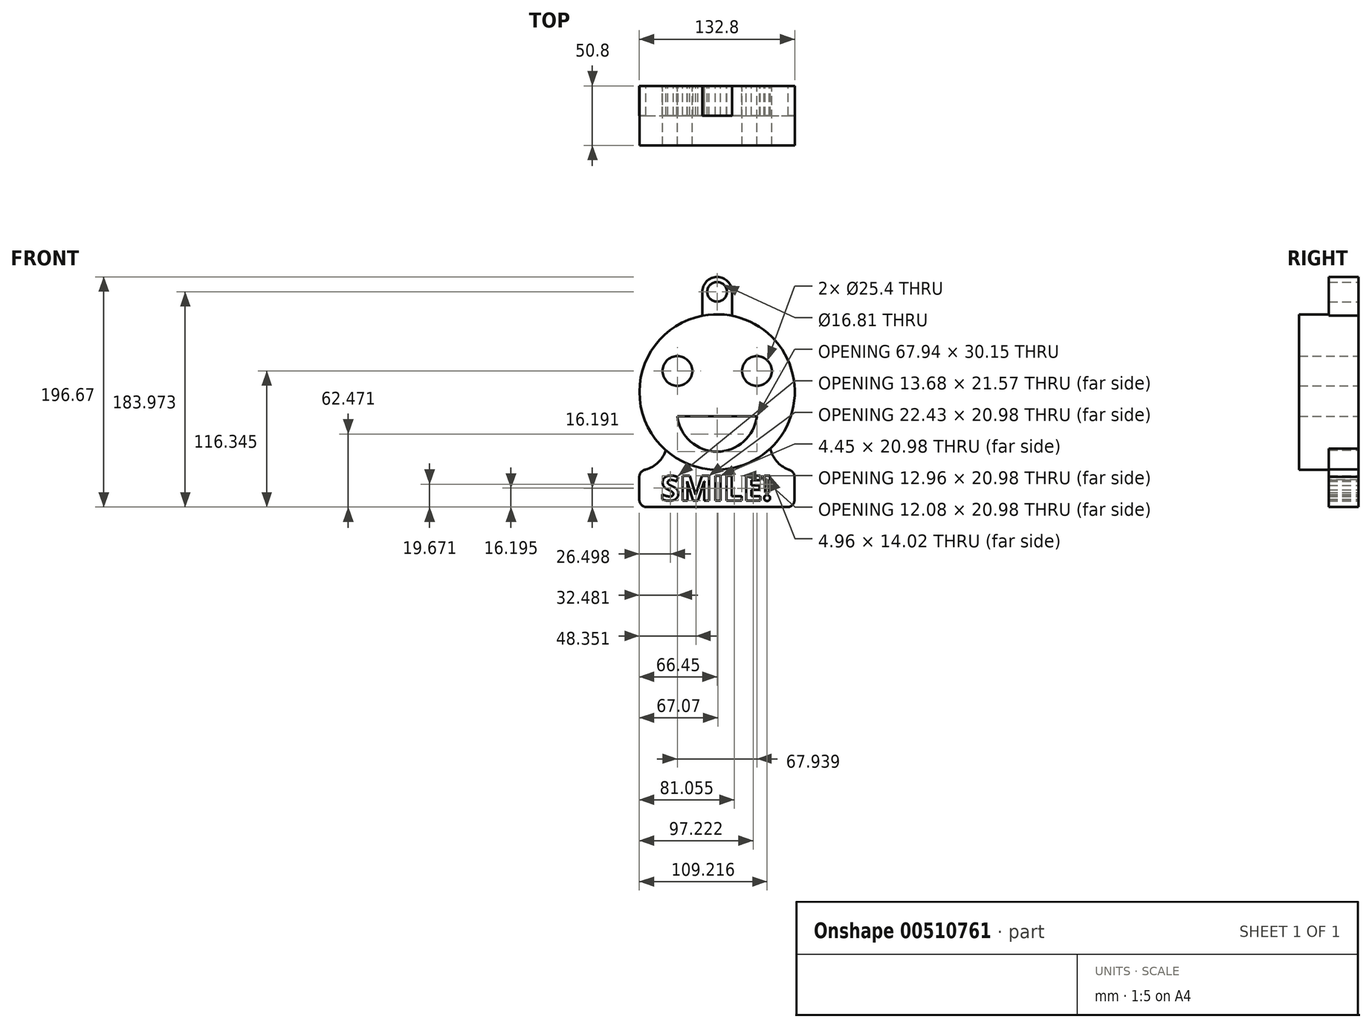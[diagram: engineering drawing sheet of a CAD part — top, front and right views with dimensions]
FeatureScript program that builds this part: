
annotation { "Feature Type Name" : "Feature", "Feature Type Description" : "" }
export const myFeature = defineFeature(function(context is Context, id is Id, definition is map)
    precondition{}
    {
        {
            var Q0;
            Q0=qCreatedBy(makeId("Front.planeOp"),FACE);
            var sketch = newSketch(context, id + "F0", { "sketchPlane" : qUnion([Q0])});
            skCircle(sketch, "E0", {"center": v(0, 0) * mm, "radius": 66.35 * mm});
            skCircle(sketch, "E1", {"center": v(-33.97, 17.93) * mm, "radius": 12.7 * mm});
            skCircle(sketch, "E2", {"center": v(33.97, 17.93) * mm, "radius": 12.7 * mm});
            skLineSegment(sketch, "E3", {"start": v(-33.97, -20.87) * mm, "end": v(33.97, -20.87) * mm});
            skArc(sketch, "E4", {"start": v(-33.97, -20.87) * mm, "mid": v(0, -51.01) * mm, "end": v(33.97, -20.87) * mm});
            skSolve(sketch);
        }
        {
            var Q0;
            Q0=makeQuery(id+"F0.imprint","IMPRINT",FACE,{"disambiguationData":[TD([[makeQuery(id+"F0.imprint","IMPRINT",EDGE,{"derivedFrom":sQuery(id+"F0.wireOp",EDGE,"E0")}),1.0]])]});
            extrude(context, id + "F1", {"entities" : qUnion([Q0]), "depth" : 25.4 * mm, "offsetDistance" : 25.4 * mm});
        }
        {
            var Q0;
            Q0=qCreatedBy(makeId("Front.planeOp"),FACE);
            var sketch = newSketch(context, id + "F2", { "sketchPlane" : qUnion([Q0])});
            skLineSegment(sketch, "E5", {"start": v(-66.45, -72.6) * mm, "end": v(-66.45, -92.06) * mm});
            skLineSegment(sketch, "E6", {"start": v(66.25, -72.6) * mm, "end": v(66.25, -92.06) * mm});
            skPoint(sketch, "E7.top.end.orphan", {"position": v(62.57, -102.89) * mm});
            skLineSegment(sketch, "E8", {"start": v(-60.1, -98.4) * mm, "end": v(59.9, -98.4) * mm});
            skLineSegment(sketch, "E9", {"start": v(66.25, -92.06) * mm, "end": v(66.25, -72.6) * mm});
            skLineSegment(sketch, "E10", {"start": v(60.65, -66.25) * mm, "end": v(-60.1, -66.25) * mm});
            skPoint(sketch, "E11.orphan", {"position": v(-66.45, 4.16) * mm});
            skPoint(sketch, "E12.orphan", {"position": v(66.25, 4.16) * mm});
            skText(sketch, "E13", { "text": "SMILE!", "fontName": "OpenSans-Bold.ttf"});
            skLineSegment(sketch, "E14", {"start": v(-12.7, 65.21) * mm, "end": v(-12.7, 85.56) * mm});
            skLineSegment(sketch, "E15", {"start": v(12.7, 64.8) * mm, "end": v(12.7, 85.56) * mm});
            skArc(sketch, "E16", {"start": v(12.7, 85.56) * mm, "mid": v(0, 98.26) * mm, "end": v(-12.7, 85.56) * mm});
            skPoint(sketch, "E17.orphan", {"position": v(0, 95.74) * mm});
            skPoint(sketch, "E18.end.orphan", {"position": v(12.7, 68.47) * mm});
            skPoint(sketch, "E19.end.orphan", {"position": v(-12.7, 68.47) * mm});
            skCircle(sketch, "E20", {"center": v(0, 85.56) * mm, "radius": 8.4 * mm});
            skPoint(sketch, "E21.visualSharp", {"position": v(-66.45, -98.4) * mm});
            skArc(sketch, "E21.filletArc", {"start": v(-66.45, -92.06) * mm, "mid": v(-64.6, -96.55) * mm, "end": v(-60.1, -98.4) * mm});
            skPoint(sketch, "E22.visualSharp", {"position": v(66.25, -98.4) * mm});
            skArc(sketch, "E22.filletArc", {"start": v(59.9, -98.4) * mm, "mid": v(64.39, -96.55) * mm, "end": v(66.25, -92.06) * mm});
            skPoint(sketch, "E23.orphan", {"position": v(66.25, -102.89) * mm});
            skPoint(sketch, "E24.start.orphan", {"position": v(45.1, -46.6) * mm});
            skPoint(sketch, "E25.end.orphan", {"position": v(-43.02, -46.6) * mm});
            skPoint(sketch, "E26.visualSharp", {"position": v(-66.45, -66.25) * mm});
            skArc(sketch, "E26.filletArc", {"start": v(-60.1, -66.25) * mm, "mid": v(-64.6, -68.11) * mm, "end": v(-66.45, -72.6) * mm});
            skArc(sketch, "E27", {"start": v(66.25, -72.6) * mm, "mid": v(63.86, -67.7) * mm, "end": v(58.6, -66.25) * mm});
            skArc(sketch, "E28", {"start": v(-62.38, -66.68) * mm, "mid": v(-49.7, -59.54) * mm, "end": v(-43.02, -46.6) * mm});
            skArc(sketch, "E29", {"start": v(45.1, -46.6) * mm, "mid": v(50.29, -58.48) * mm, "end": v(60.65, -66.25) * mm});
            skLineSegment(sketch, "E30", {"start": v(-12.7, 65.21) * mm, "end": v(12.7, 64.8) * mm});
            skLineSegment(sketch, "E31", {"start": v(-43.02, -46.6) * mm, "end": v(0, -60.5) * mm});
            skLineSegment(sketch, "E32", {"start": v(0, -60.5) * mm, "end": v(45.1, -46.6) * mm});
            const initialGuessF2  = {"E13": [-0.04814, -0.09271, 1, 0, 0.02116]};
            skSetInitialGuess(sketch, initialGuessF2);
            skSolve(sketch);
        }
        {
            var Q0;
            Q0=makeQuery(id+"F1.opExtrude","CAP_FACE",FACE,{"disambiguationData":[OSD([sQuery(id+"F0.wireOp",EDGE,"E0"),sQuery(id+"F0.wireOp",EDGE,"E1"),sQuery(id+"F0.wireOp",EDGE,"E2"),sQuery(id+"F0.wireOp",EDGE,"E3"),sQuery(id+"F0.wireOp",EDGE,"E4")])],"isStart":false});
            var Q1;
            Q1=makeQuery(id+"F1.opExtrude","CAP_FACE",FACE,{"disambiguationData":[OSD([sQuery(id+"F0.wireOp",EDGE,"E0"),sQuery(id+"F0.wireOp",EDGE,"E1"),sQuery(id+"F0.wireOp",EDGE,"E2"),sQuery(id+"F0.wireOp",EDGE,"E3"),sQuery(id+"F0.wireOp",EDGE,"E4")])],"isStart":true});
            var Q2;
            Q2 = qSketchRegion(id + "F2", true);
            extrude(context, id + "F3", {"entities" : qUnion([Q0, Q1, Q2]), "operationType" : NewBodyOperationType.ADD, "depth" : 25.4 * mm, "offsetDistance" : 25.4 * mm});
        }
    });
